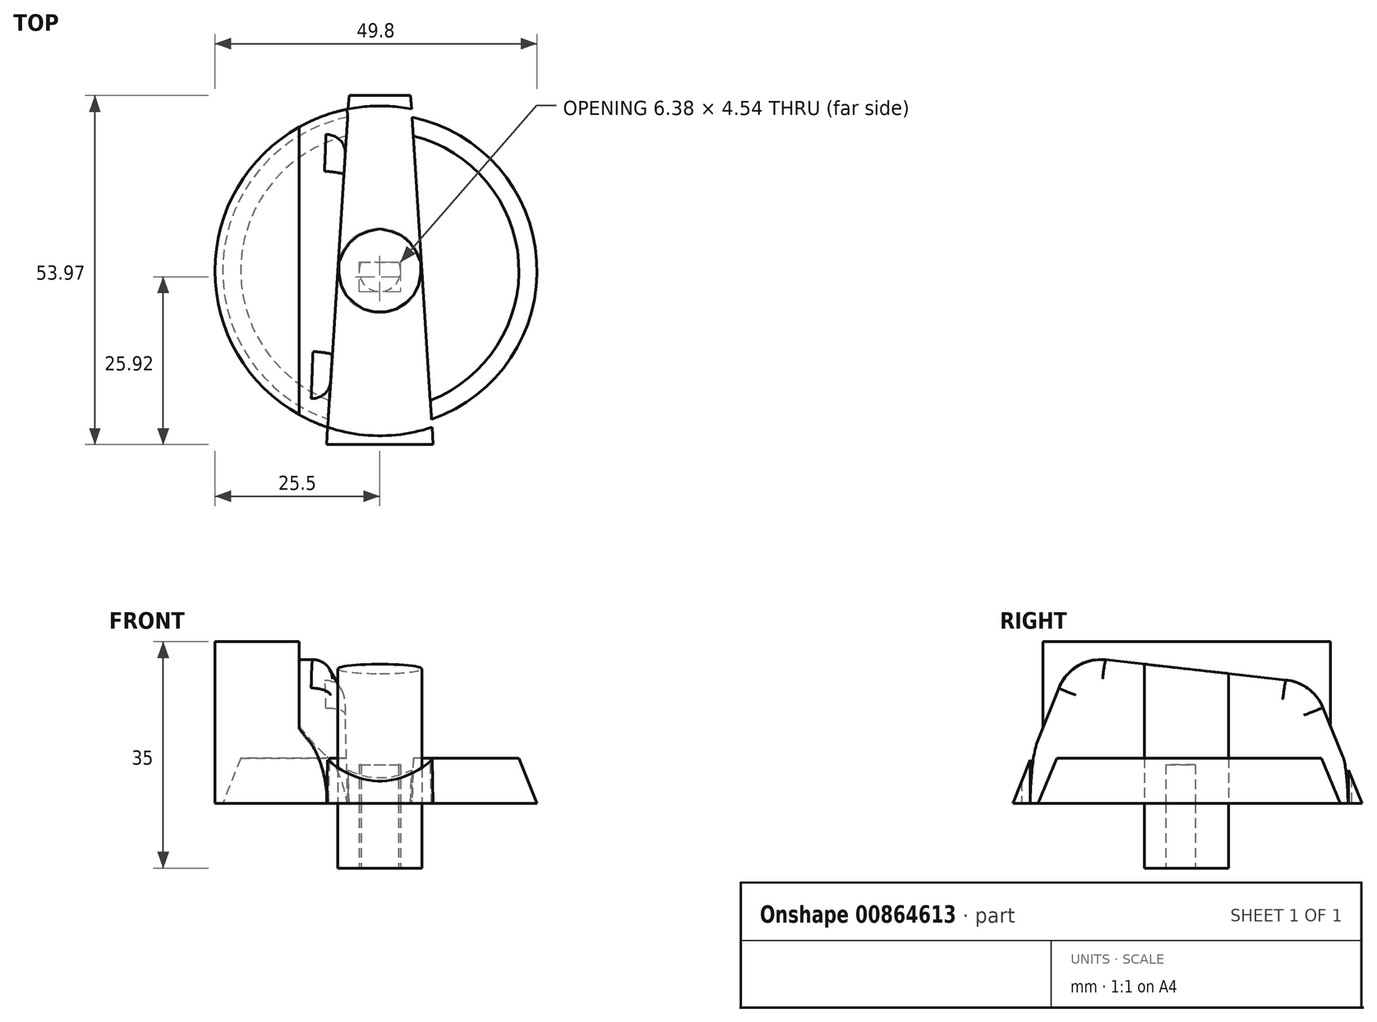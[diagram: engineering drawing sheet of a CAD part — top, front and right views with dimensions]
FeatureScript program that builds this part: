
annotation { "Feature Type Name" : "Feature", "Feature Type Description" : "" }
export const myFeature = defineFeature(function(context is Context, id is Id, definition is map)
    precondition{}
    {
        {
            var Q0;
            Q0=qCreatedBy(makeId("Top.planeOp"),FACE);
            var sketch = newSketch(context, id + "F0", { "sketchPlane" : qUnion([Q0])});
            skCircle(sketch, "E0", {"center": v(0, 0) * mm, "radius": 6.5 * mm});
            skArc(sketch, "E1", {"start": v(-2.9, 1.34) * mm, "mid": v(0, -3.2) * mm, "end": v(2.9, 1.34) * mm});
            skLineSegment(sketch, "E2.top", {"start": v(-2.9, 1.34) * mm, "end": v(2.9, 1.34) * mm});
            skSolve(sketch);
        }
        {
            var Q0;
            Q0=makeQuery(id+"F0.imprint","IMPRINT",FACE,{"disambiguationData":[TD([[makeQuery(id+"F0.imprint","IMPRINT",EDGE,{"derivedFrom":sQuery(id+"F0.wireOp",EDGE,"E0")}),1.0]])]});
            extrude(context, id + "F1", {"entities" : qUnion([Q0]), "depth" : 10 * mm, "offsetDistance" : 25 * mm});
        }
        {
            var Q0;
            Q0=makeQuery(id+"F1.opExtrude","CAP_FACE",FACE,{"disambiguationData":[OSD([sQuery(id+"F0.wireOp",EDGE,"E0"),sQuery(id+"F0.wireOp",EDGE,"E1"),sQuery(id+"F0.wireOp",EDGE,"E2.top")])],"isStart":false});
            var sketch = newSketch(context, id + "F2", { "sketchPlane" : qUnion([Q0])});
            skCircle(sketch, "E3", {"center": v(0, 0) * mm, "radius": 25.5 * mm});
            skCircle(sketch, "E4.0", {"center": v(0, 0) * mm, "radius": 6.5 * mm});
            skArc(sketch, "E4.1", {"start": v(-2.9, 1.34) * mm, "mid": v(0, -3.2) * mm, "end": v(2.9, 1.34) * mm});
            skLineSegment(sketch, "E5.bottom", {"start": v(-4.76, 27.15) * mm, "end": v(4.76, 27.15) * mm});
            skLineSegment(sketch, "E5.top", {"start": v(-8.25, -26.85) * mm, "end": v(8.25, -26.85) * mm});
            skLineSegment(sketch, "E6", {"start": v(-8.25, -26.85) * mm, "end": v(-4.76, 27.15) * mm});
            skLineSegment(sketch, "E7", {"start": v(8.25, -26.85) * mm, "end": v(4.76, 27.15) * mm});
            skSolve(sketch);
        }
        {
            var Q0;
            Q0=makeQuery(id+"F2.imprint","IMPRINT",FACE,{"disambiguationData":[TD([[makeQuery(id+"F2.imprint","IMPRINT",EDGE,{"derivedFrom":makeQuery(id+"F1.opExtrude","CAP_EDGE",EDGE,{"disambiguationData":[OSD([sQuery(id+"F0.wireOp",EDGE,"E0")])],"isStart":false})}),1.0]])]});
            var Q1;
            Q1=makeQuery(id+"F2.imprint","IMPRINT",FACE,{"disambiguationData":[TD([[makeQuery(id+"F2.imprint","IMPRINT",EDGE,{"derivedFrom":makeQuery(id+"F1.opExtrude","CAP_EDGE",EDGE,{"disambiguationData":[OSD([sQuery(id+"F0.wireOp",EDGE,"E1")])],"isStart":false})}),1.0]])]});
            var Q2;
            Q2=makeQuery(id+"F2.imprint","IMPRINT",FACE,{"disambiguationData":[TD([[makeQuery(id+"F2.imprint","IMPRINT",EDGE,{"derivedFrom":sQuery(id+"F2.wireOp",EDGE,"E3")}),1.0]])]});
            extrude(context, id + "F3", {"entities" : qUnion([Q0, Q1, Q2]), "operationType" : NewBodyOperationType.ADD, "depth" : 7 * mm, "offsetDistance" : 25 * mm});
        }
        {
            var Q0;
            Q0=makeQuery(id+"F3.opExtrude","CAP_EDGE",EDGE,{"disambiguationData":[OSD([sQuery(id+"F2.wireOp",EDGE,"E3")])],"isStart":false});
            chamfer(context, id + "F4", {"entities" : qUnion([Q0]), "chamferType" : ChamferType.TWO_OFFSETS, "width1" : 4 * mm, "oppositeDirection" : false, "width2" : 10 * mm, "tangentPropagation" : true});
        }
        {
            var Q0;
            Q0=makeQuery(id+"F2.imprint","IMPRINT",FACE,{"disambiguationData":[TD([[makeQuery(id+"F2.imprint","IMPRINT",EDGE,{"derivedFrom":sQuery(id+"F2.wireOp",EDGE,"E4.1")}),1.0]])]});
            var Q1;
            Q1=makeQuery(id+"F2.imprint","IMPRINT",FACE,{"disambiguationData":[TD([[makeQuery(id+"F2.imprint","IMPRINT",EDGE,{"derivedFrom":sQuery(id+"F2.wireOp",EDGE,"E4.1")}),-1.0]])]});
            var Q2;
            {var subQ0=sQuery(id+"F2.wireOp",EDGE,"E6");var subQ1=sQuery(id+"F2.wireOp",EDGE,"E3");var subQ2=makeQuery(id+"F2.imprint","INTERSECT",VERTEX,{"disambiguationData":[OD(0.0)],"derivedFrom":[subQ1,subQ0]});Q2=makeQuery(id+"F2.imprint","IMPRINT",FACE,{"disambiguationData":[TD([[makeQuery(id+"F2.imprint","IMPRINT",EDGE,{"disambiguationData":[TD([[subQ2,1.0]])],"derivedFrom":subQ1}),1.0]])]});}
            var Q3;
            {var subQ5=sQuery(id+"F2.wireOp",EDGE,"E5.bottom");Q3=makeQuery(id+"F2.imprint","IMPRINT",FACE,{"disambiguationData":[TD([[makeQuery(id+"F2.imprint","IMPRINT",EDGE,{"derivedFrom":subQ5}),-1.0]])]});}
            var Q4;
            {var subQ0=sQuery(id+"F2.wireOp",EDGE,"E6");var subQ1=sQuery(id+"F2.wireOp",EDGE,"E3");var subQ2=makeQuery(id+"F2.imprint","INTERSECT",VERTEX,{"disambiguationData":[OD(1.0)],"derivedFrom":[subQ1,subQ0]});Q4=makeQuery(id+"F2.imprint","IMPRINT",FACE,{"disambiguationData":[TD([[makeQuery(id+"F2.imprint","IMPRINT",EDGE,{"disambiguationData":[TD([[subQ2,-1.0]])],"derivedFrom":subQ1}),1.0]])]});}
            var Q5;
            {var subQ5=sQuery(id+"F2.wireOp",EDGE,"E5.top");Q5=makeQuery(id+"F2.imprint","IMPRINT",FACE,{"disambiguationData":[TD([[makeQuery(id+"F2.imprint","IMPRINT",EDGE,{"derivedFrom":subQ5}),1.0]])]});}
            extrude(context, id + "F5", {"entities" : qUnion([Q0, Q1, Q2, Q3, Q4, Q5]), "depth" : 25 * mm, "offsetDistance" : 25 * mm});
        }
        {
            var Q0;
            Q0=makeQuery(id+"F2.imprint","IMPRINT",FACE,{"disambiguationData":[TD([[makeQuery(id+"F2.imprint","IMPRINT",EDGE,{"derivedFrom":sQuery(id+"F2.wireOp",EDGE,"E4.1")}),1.0]])]});
            extrude(context, id + "F6", {"entities" : qUnion([Q0]), "operationType" : NewBodyOperationType.REMOVE, "depth" : 6 * mm, "offsetDistance" : 25 * mm});
        }
        {
            var Q0;
            Q0=qCreatedBy(makeId("Right.planeOp"),FACE);
            var sketch = newSketch(context, id + "F7", { "sketchPlane" : qUnion([Q0])});
            skLineSegment(sketch, "E8", {"start": v(-26.9, 9.93) * mm, "end": v(-19.75, 27.84) * mm});
            skLineSegment(sketch, "E9", {"start": v(-12.47, 32.2) * mm, "end": v(15.4, 29.08) * mm});
            skLineSegment(sketch, "E10", {"start": v(21.11, 24.77) * mm, "end": v(27.14, 9.93) * mm});
            skLineSegment(sketch, "E11", {"start": v(27.14, 9.93) * mm, "end": v(30.82, 12.15) * mm});
            skLineSegment(sketch, "E12", {"start": v(30.82, 12.15) * mm, "end": v(31.39, 37.87) * mm});
            skLineSegment(sketch, "E13", {"start": v(31.39, 37.87) * mm, "end": v(20.5, 41.16) * mm});
            skLineSegment(sketch, "E14", {"start": v(20.5, 41.16) * mm, "end": v(-34.12, 41.16) * mm});
            skLineSegment(sketch, "E15", {"start": v(-34.12, 41.16) * mm, "end": v(-29.62, 14.5) * mm});
            skLineSegment(sketch, "E16", {"start": v(-29.62, 14.5) * mm, "end": v(-29.62, 9.62) * mm});
            skLineSegment(sketch, "E17", {"start": v(-29.62, 9.62) * mm, "end": v(-26.9, 9.93) * mm});
            skPoint(sketch, "E18.visualSharp", {"position": v(-17.77, 32.8) * mm});
            skArc(sketch, "E18.filletArc", {"start": v(-12.47, 32.2) * mm, "mid": v(-16.84, 31.26) * mm, "end": v(-19.75, 27.84) * mm});
            skPoint(sketch, "E19.visualSharp", {"position": v(19.54, 28.62) * mm});
            skArc(sketch, "E19.filletArc", {"start": v(21.11, 24.77) * mm, "mid": v(18.85, 27.7) * mm, "end": v(15.4, 29.08) * mm});
            skSolve(sketch);
        }
        {
            var Q0;
            Q0=makeQuery(id+"F7.imprint","IMPRINT",FACE,{"disambiguationData":[TD([[makeQuery(id+"F7.imprint","IMPRINT",EDGE,{"derivedFrom":sQuery(id+"F7.wireOp",EDGE,"E8")}),1.0]])]});
            extrude(context, id + "F8", {"entities" : qUnion([Q0]), "operationType" : NewBodyOperationType.REMOVE, "endBound" : BoundingType.SYMMETRIC, "oppositeDirection" : true, "depth" : 25 * mm, "offsetDistance" : 25 * mm});
        }
        {
            var Q0;
            Q0=makeQuery(id+"F8.boolean.opBoolean","INTERSECT",EDGE,{"derivedFrom":[makeQuery(id+"F5.opExtrude","SWEPT_FACE",FACE,{"disambiguationData":[OSD([sQuery(id+"F2.wireOp",EDGE,"E7")])]}),makeQuery(id+"F8.opExtrude","SWEPT_FACE",FACE,{"disambiguationData":[OSD([sQuery(id+"F7.wireOp",EDGE,"E9")])]})]});
            var Q1;
            Q1=makeQuery(id+"F8.boolean.opBoolean","INTERSECT",EDGE,{"derivedFrom":[makeQuery(id+"F5.opExtrude","SWEPT_FACE",FACE,{"disambiguationData":[OSD([sQuery(id+"F2.wireOp",EDGE,"E6")])]}),makeQuery(id+"F8.opExtrude","SWEPT_FACE",FACE,{"disambiguationData":[OSD([sQuery(id+"F7.wireOp",EDGE,"E9")])]})]});
            var Q2;
            {var subQ0=sQuery(id+"F2.wireOp",EDGE,"E6");var subQ1=sQuery(id+"F2.wireOp",EDGE,"E3");Q2=makeQuery(id+"F4.opChamfer","BLEND_EDGE",EDGE,{"blendedFrom":[makeQuery(id+"F3.opExtrude","CAP_EDGE",EDGE,{"disambiguationData":[OSD([subQ1]),TDD([makeQuery(id+"F2.imprint","IMPRINT",EDGE,{"disambiguationData":[TD([[makeQuery(id+"F2.imprint","INTERSECT",VERTEX,{"disambiguationData":[OD(0.0)],"derivedFrom":[subQ1,subQ0]}),-1.0]])],"derivedFrom":subQ1})])],"isStart":false}),makeQuery(id+"F3.opExtrude","CAP_FACE",FACE,{"disambiguationData":[OSD([subQ1,subQ0])],"isStart":false})],"blendedInto":[makeQuery(id+"F3.opExtrude","CAP_FACE",FACE,{"disambiguationData":[OSD([subQ1,subQ0])],"isStart":false})]});}
            var Q3;
            {var subQ0=sQuery(id+"F2.wireOp",EDGE,"E7");var subQ1=sQuery(id+"F2.wireOp",EDGE,"E3");Q3=makeQuery(id+"F4.opChamfer","BLEND_EDGE",EDGE,{"blendedFrom":[makeQuery(id+"F3.opExtrude","CAP_EDGE",EDGE,{"disambiguationData":[OSD([subQ1]),TDD([makeQuery(id+"F2.imprint","IMPRINT",EDGE,{"disambiguationData":[TD([[makeQuery(id+"F2.imprint","INTERSECT",VERTEX,{"disambiguationData":[OD(0.0)],"derivedFrom":[subQ1,subQ0]}),1.0]])],"derivedFrom":subQ1})])],"isStart":false}),makeQuery(id+"F3.opExtrude","CAP_FACE",FACE,{"disambiguationData":[OSD([subQ1,subQ0])],"isStart":false})],"blendedInto":[makeQuery(id+"F3.opExtrude","CAP_FACE",FACE,{"disambiguationData":[OSD([subQ1,subQ0])],"isStart":false})]});}
            fillet(context, id + "F9", {"entities" : qUnion([Q0, Q1, Q2, Q3]), "radius" : 3 * mm, "tangentPropagation" : true, "allowEdgeOverflow" : false});
        }
    });
